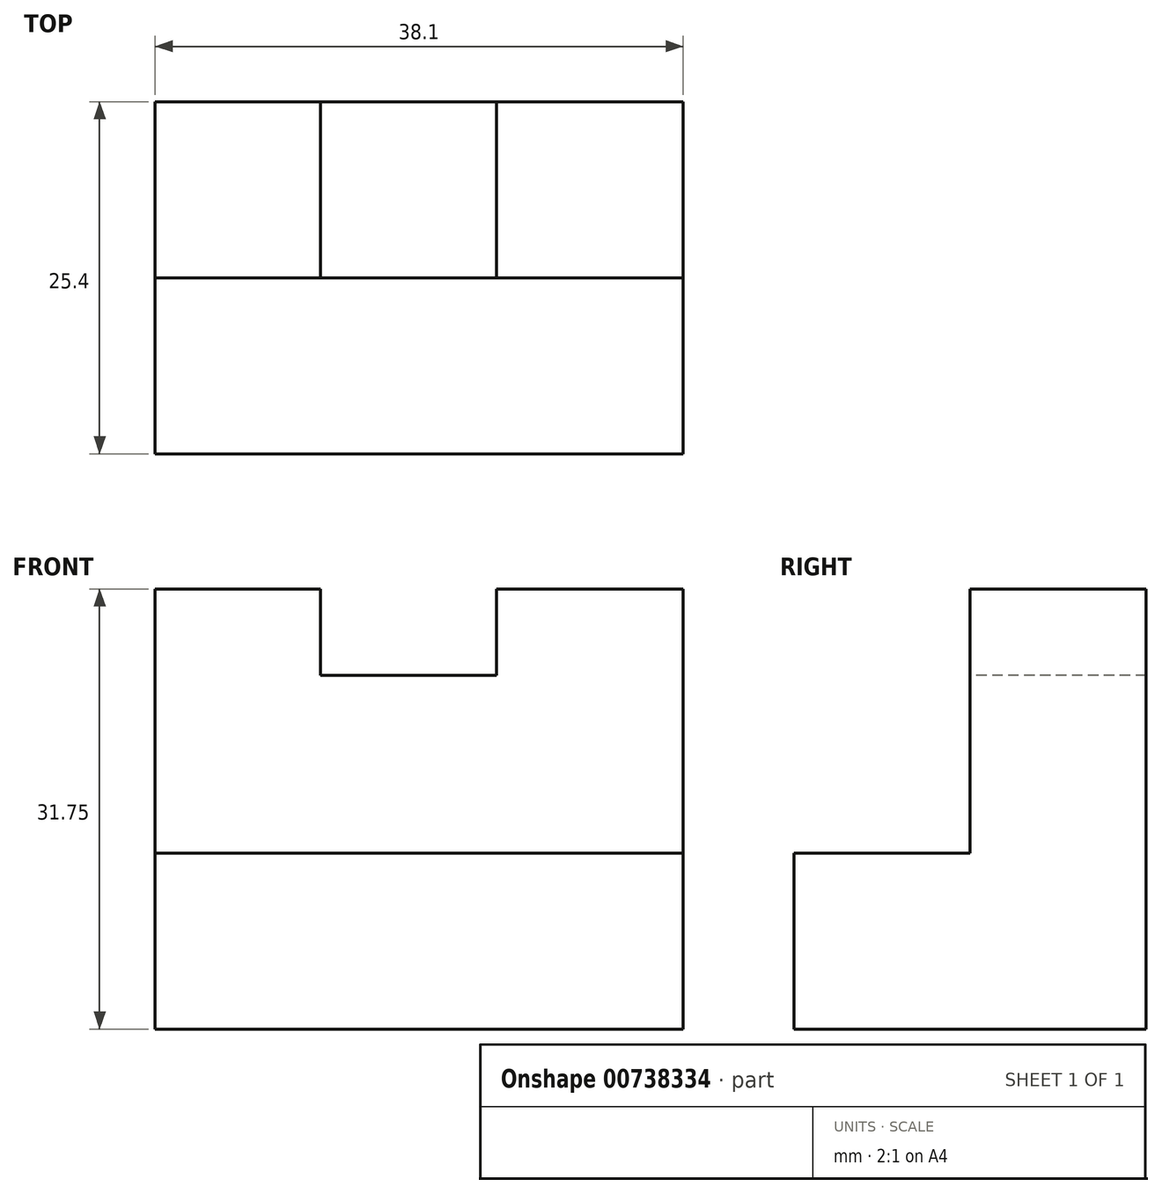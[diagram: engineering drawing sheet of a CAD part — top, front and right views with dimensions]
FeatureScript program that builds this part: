
annotation { "Feature Type Name" : "Feature", "Feature Type Description" : "" }
export const myFeature = defineFeature(function(context is Context, id is Id, definition is map)
    precondition{}
    {
        {
            var Q0;
            Q0=qCreatedBy(makeId("Right.planeOp"),FACE);
            var sketch = newSketch(context, id + "F0", { "sketchPlane" : qUnion([Q0])});
            skLineSegment(sketch, "E0", {"start": v(0, 0) * mm, "end": v(25.4, 0) * mm});
            skLineSegment(sketch, "E1", {"start": v(25.4, 0) * mm, "end": v(25.4, 31.75) * mm});
            skLineSegment(sketch, "E2", {"start": v(25.4, 31.75) * mm, "end": v(12.7, 31.75) * mm});
            skLineSegment(sketch, "E3", {"start": v(12.7, 31.75) * mm, "end": v(12.7, 12.7) * mm});
            skLineSegment(sketch, "E4", {"start": v(12.7, 12.7) * mm, "end": v(0, 12.7) * mm});
            skLineSegment(sketch, "E5", {"start": v(0, 12.7) * mm, "end": v(0, 0) * mm});
            skSolve(sketch);
        }
        {
            var Q0;
            Q0 = qSketchRegion(id + "F0", true);
            extrude(context, id + "F1", {"entities" : qUnion([Q0]), "depth" : 38.1 * mm, "offsetDistance" : 25.4 * mm});
        }
        {
            var Q0;
            Q0=qCreatedBy(makeId("Front.planeOp"),FACE);
            var sketch = newSketch(context, id + "F2", { "sketchPlane" : qUnion([Q0])});
            skLineSegment(sketch, "E6", {"start": v(11.94, 31.87) * mm, "end": v(11.94, 25.52) * mm});
            skLineSegment(sketch, "E7", {"start": v(11.94, 25.52) * mm, "end": v(24.64, 25.52) * mm});
            skLineSegment(sketch, "E8", {"start": v(24.64, 25.52) * mm, "end": v(24.64, 31.87) * mm});
            skLineSegment(sketch, "E9", {"start": v(24.64, 31.87) * mm, "end": v(11.94, 31.87) * mm});
            skSolve(sketch);
        }
        {
            var Q0;
            Q0 = qSketchRegion(id + "F2", true);
            extrude(context, id + "F3", {"entities" : qUnion([Q0]), "operationType" : NewBodyOperationType.REMOVE, "endBound" : BoundingType.THROUGH_ALL, "oppositeDirection" : true, "depth" : 12.7 * mm, "offsetDistance" : 25.4 * mm});
        }
    });
